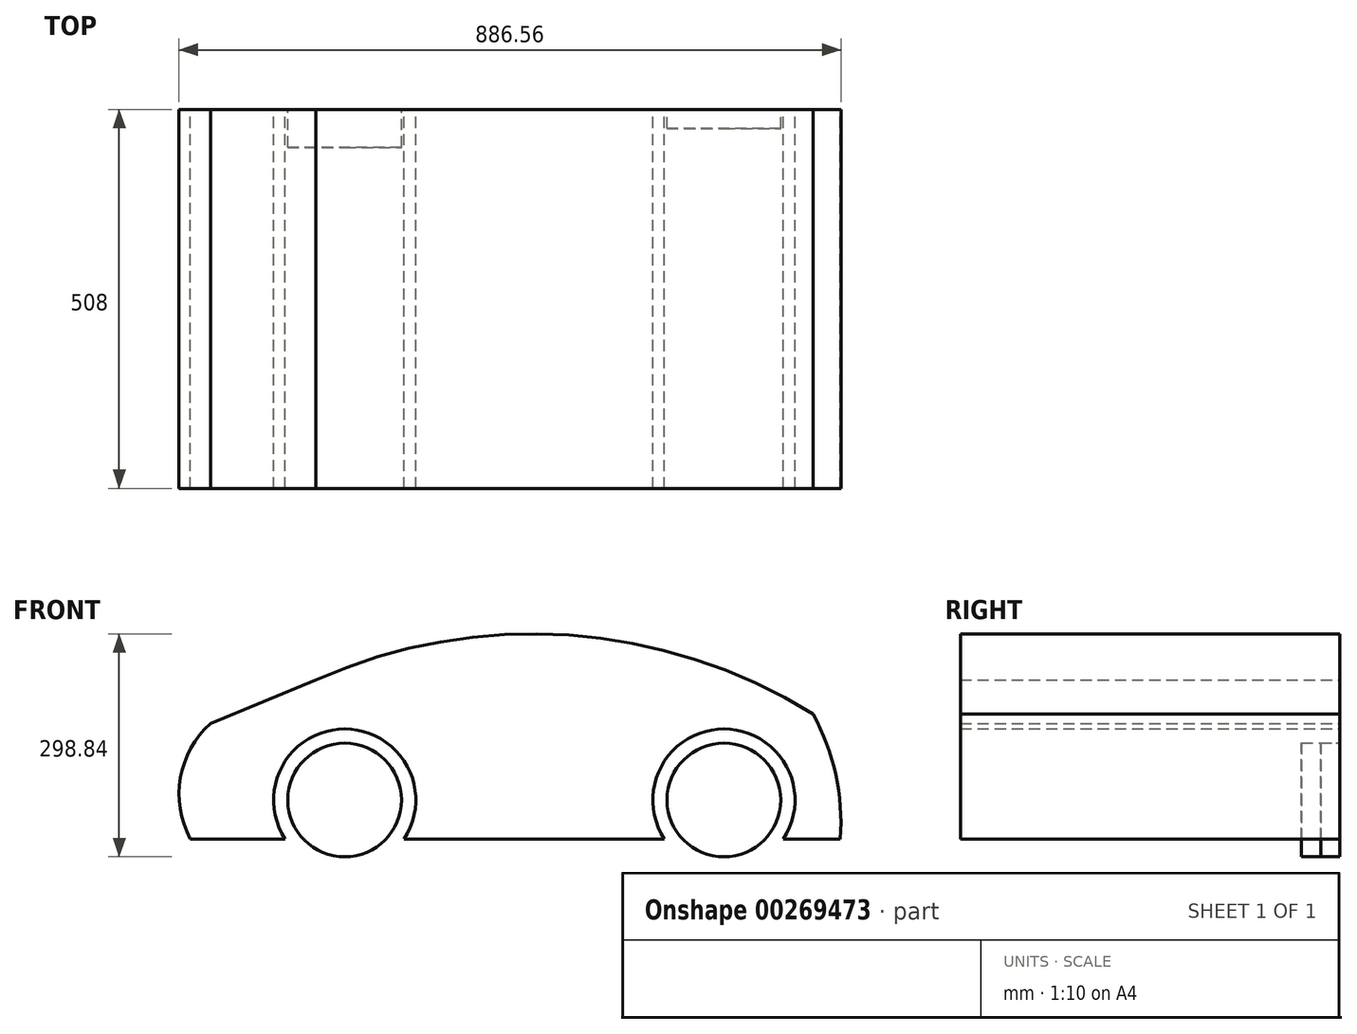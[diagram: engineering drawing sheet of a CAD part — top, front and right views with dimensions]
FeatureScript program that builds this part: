
annotation { "Feature Type Name" : "Feature", "Feature Type Description" : "" }
export const myFeature = defineFeature(function(context is Context, id is Id, definition is map)
    precondition{}
    {
        {
            var Q0;
            Q0=qCreatedBy(makeId("Front.planeOp"),FACE);
            var sketch = newSketch(context, id + "F0", { "sketchPlane" : qUnion([Q0])});
            skCircle(sketch, "E0", {"center": v(-254, 0) * mm, "radius": 76.2 * mm});
            skCircle(sketch, "E1", {"center": v(254, 0) * mm, "radius": 76.2 * mm});
            skLineSegment(sketch, "E2", {"start": v(-254, 0) * mm, "end": v(254, 0) * mm, "construction": true});
            skLineSegment(sketch, "E3", {"start": v(-174.3, -52.16) * mm, "end": v(174.3, -52.16) * mm});
            skArc(sketch, "E4", {"start": v(333.7, -52.16) * mm, "mid": v(254, 95.25) * mm, "end": v(174.3, -52.16) * mm});
            skArc(sketch, "E5", {"start": v(-174.3, -52.16) * mm, "mid": v(-254, 95.25) * mm, "end": v(-333.7, -52.16) * mm});
            skLineSegment(sketch, "E6", {"start": v(-333.7, -52.16) * mm, "end": v(-460.7, -52.16) * mm});
            skArc(sketch, "E7", {"start": v(-433.78, 102.58) * mm, "mid": v(-474.03, 29.87) * mm, "end": v(-460.7, -52.16) * mm});
            skLineSegment(sketch, "E8", {"start": v(333.7, -52.16) * mm, "end": v(409.9, -52.16) * mm});
            skLineSegment(sketch, "E9", {"start": v(-433.78, 102.58) * mm, "end": v(-292.4, 160.9) * mm});
            skArc(sketch, "E10", {"start": v(373.51, 115.07) * mm, "mid": v(46.26, 220.96) * mm, "end": v(-292.4, 160.9) * mm});
            skPoint(sketch, "E11.end.orphan", {"position": v(511.5, 0) * mm});
            skArc(sketch, "E12", {"start": v(409.9, -52.16) * mm, "mid": v(403.68, 34.06) * mm, "end": v(373.51, 115.07) * mm});
            skSolve(sketch);
        }
        {
            var Q0;
            Q0=makeQuery(id+"F0.imprint","IMPRINT",FACE,{"disambiguationData":[TD([[makeQuery(id+"F0.imprint","IMPRINT",EDGE,{"derivedFrom":sQuery(id+"F0.wireOp",EDGE,"E3")}),1.0]])]});
            extrude(context, id + "F1", {"entities" : qUnion([Q0]), "depth" : 508 * mm});
        }
        {
            var Q0;
            Q0 = qSketchRegion(id + "F0", true);
            extrude(context, id + "F2", {"entities" : qUnion([Q0]), "operationType" : NewBodyOperationType.ADD, "depth" : 25.4 * mm});
        }
        {
            var Q0;
            Q0=makeQuery(id+"F2.opExtrude","CAP_FACE",FACE,{"disambiguationData":[OSD([sQuery(id+"F0.wireOp",EDGE,"E0")])],"isStart":false});
            var sketch = newSketch(context, id + "F3", { "sketchPlane" : qUnion([Q0])});
            skCircle(sketch, "E13", {"center": v(-254, 0) * mm, "radius": 76.2 * mm});
            skSolve(sketch);
        }
        {
            var Q0;
            Q0=makeQuery(id+"F3.imprint","IMPRINT",FACE,{"disambiguationData":[TD([[makeQuery(id+"F3.imprint","IMPRINT",EDGE,{"derivedFrom":sQuery(id+"F3.wireOp",EDGE,"E13")}),1.0]])]});
            extrude(context, id + "F4", {"entities" : qUnion([Q0]), "operationType" : NewBodyOperationType.ADD, "depth" : 25.4 * mm});
        }
    });
